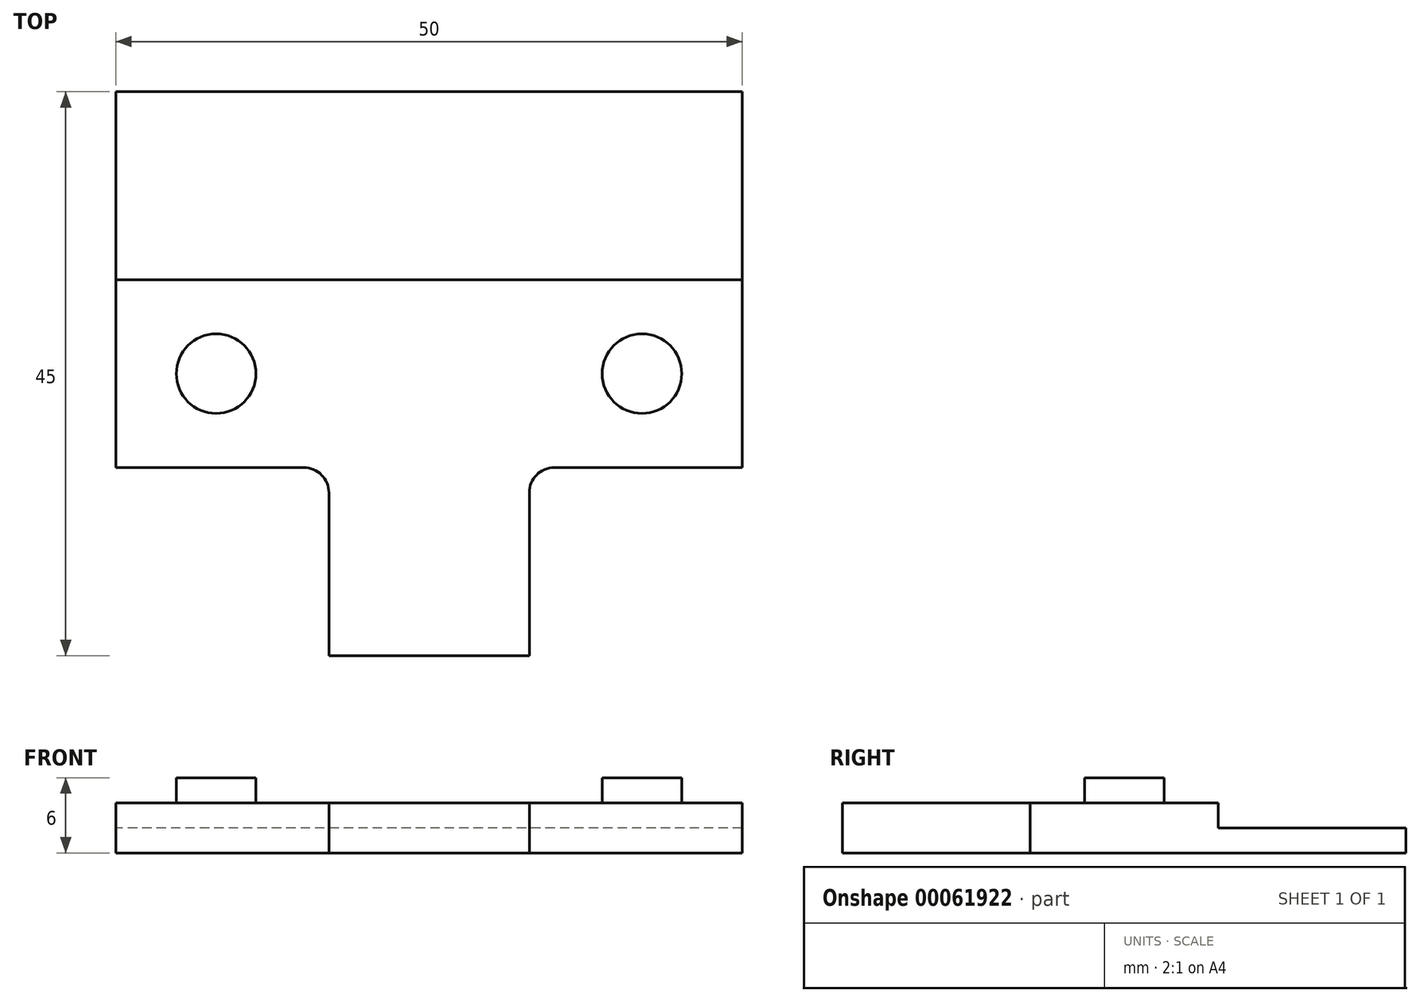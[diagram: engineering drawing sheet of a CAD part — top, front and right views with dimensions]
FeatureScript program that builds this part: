
annotation { "Feature Type Name" : "Feature", "Feature Type Description" : "" }
export const myFeature = defineFeature(function(context is Context, id is Id, definition is map)
    precondition{}
    {
        {
            var Q0;
            Q0=qCreatedBy(makeId("Top.planeOp"),FACE);
            var sketch = newSketch(context, id + "F0", { "sketchPlane" : qUnion([Q0])});
            skLineSegment(sketch, "E0.rect.bottom", {"start": v(8, -15) * mm, "end": v(-8, -15) * mm});
            skLineSegment(sketch, "E0.rect.top", {"start": v(25, 15) * mm, "end": v(-25, 15) * mm});
            skLineSegment(sketch, "E0.rect.left", {"start": v(25, 0) * mm, "end": v(25, 15) * mm});
            skLineSegment(sketch, "E0.rect.right", {"start": v(-25, 0) * mm, "end": v(-25, 15) * mm});
            skPoint(sketch, "E0.rect.middle", {"position": v(0, 0) * mm});
            skLineSegment(sketch, "E1", {"start": v(-25, 0) * mm, "end": v(-8, 0) * mm});
            skPoint(sketch, "E1.endSnap0", {"position": v(-25, 0) * mm});
            skLineSegment(sketch, "E2", {"start": v(-8, 0) * mm, "end": v(-8, -15) * mm});
            skLineSegment(sketch, "E3", {"start": v(25, 0) * mm, "end": v(8, 0) * mm});
            skPoint(sketch, "E3.endSnap0", {"position": v(25, 0) * mm});
            skLineSegment(sketch, "E4", {"start": v(8, 0) * mm, "end": v(8, -15) * mm});
            skPoint(sketch, "E5.orphan", {"position": v(-25, -15) * mm});
            skPoint(sketch, "E6.orphan", {"position": v(25, -15) * mm});
            skSolve(sketch);
        }
        {
            var Q0;
            Q0=makeQuery(id+"F0.imprint","IMPRINT",FACE,{"disambiguationData":[TD([[makeQuery(id+"F0.imprint","IMPRINT",EDGE,{"derivedFrom":sQuery(id+"F0.wireOp",EDGE,"E0.rect.bottom")}),-1.0]])]});
            extrude(context, id + "F1", {"entities" : qUnion([Q0]), "depth" : 2 * mm});
        }
        {
            var Q0;
            Q0=makeQuery(id+"F1.opExtrude","SWEPT_EDGE",EDGE,{"disambiguationData":[OSD([sQuery(id+"F0.wireOp",EDGE,"E1"),sQuery(id+"F0.wireOp",EDGE,"E2")])]});
            var Q1;
            Q1=makeQuery(id+"F1.opExtrude","SWEPT_EDGE",EDGE,{"disambiguationData":[OSD([sQuery(id+"F0.wireOp",EDGE,"E3"),sQuery(id+"F0.wireOp",EDGE,"E4")])]});
            fillet(context, id + "F2", {"entities" : qUnion([Q0, Q1]), "radius" : 2 * mm, "tangentPropagation" : true, "allowEdgeOverflow" : false});
        }
        {
            var Q0;
            Q0=makeQuery(id+"F1.opExtrude","CAP_FACE",FACE,{"disambiguationData":[OSD([sQuery(id+"F0.wireOp",EDGE,"E0.rect.bottom"),sQuery(id+"F0.wireOp",EDGE,"E0.rect.top"),sQuery(id+"F0.wireOp",EDGE,"E0.rect.left"),sQuery(id+"F0.wireOp",EDGE,"E0.rect.right"),sQuery(id+"F0.wireOp",EDGE,"E1"),sQuery(id+"F0.wireOp",EDGE,"E2"),sQuery(id+"F0.wireOp",EDGE,"E3"),sQuery(id+"F0.wireOp",EDGE,"E4")])],"isStart":false});
            var sketch = newSketch(context, id + "F3", { "sketchPlane" : qUnion([Q0])});
            skLineSegment(sketch, "E7", {"start": v(-25, 7.5) * mm, "end": v(-17, 7.5) * mm});
            skLineSegment(sketch, "E8", {"start": v(25, 7.5) * mm, "end": v(17, 7.5) * mm});
            skCircle(sketch, "E9", {"center": v(-17, 7.5) * mm, "radius": 3.17 * mm});
            skCircle(sketch, "E10", {"center": v(17, 7.5) * mm, "radius": 3.17 * mm});
            skSolve(sketch);
        }
        {
            var Q0;
            Q0=makeQuery(id+"F3.imprint","IMPRINT",FACE,{"disambiguationData":[TD([[makeQuery(id+"F3.imprint","IMPRINT",EDGE,{"derivedFrom":sQuery(id+"F3.wireOp",EDGE,"E9")}),1.0]])]});
            var Q1;
            Q1=makeQuery(id+"F3.imprint","IMPRINT",FACE,{"disambiguationData":[TD([[makeQuery(id+"F3.imprint","IMPRINT",EDGE,{"derivedFrom":sQuery(id+"F3.wireOp",EDGE,"E10")}),1.0]])]});
            extrude(context, id + "F4", {"entities" : qUnion([Q0, Q1]), "operationType" : NewBodyOperationType.ADD, "depth" : 2 * mm});
        }
        {
            var Q0;
            Q0=makeQuery(id+"F1.opExtrude","CAP_FACE",FACE,{"disambiguationData":[OSD([sQuery(id+"F0.wireOp",EDGE,"E0.rect.bottom"),sQuery(id+"F0.wireOp",EDGE,"E0.rect.top"),sQuery(id+"F0.wireOp",EDGE,"E0.rect.left"),sQuery(id+"F0.wireOp",EDGE,"E0.rect.right"),sQuery(id+"F0.wireOp",EDGE,"E1"),sQuery(id+"F0.wireOp",EDGE,"E2"),sQuery(id+"F0.wireOp",EDGE,"E3"),sQuery(id+"F0.wireOp",EDGE,"E4")])],"isStart":true});
            var sketch = newSketch(context, id + "F5", { "sketchPlane" : qUnion([Q0])});
            skLineSegment(sketch, "E11.0", {"start": v(8, 15) * mm, "end": v(-8, 15) * mm});
            skLineSegment(sketch, "E12.0", {"start": v(-8, 2) * mm, "end": v(-8, 15) * mm});
            skArc(sketch, "E13.0", {"start": v(-8, 2) * mm, "mid": v(-8.59, 0.59) * mm, "end": v(-10, 0) * mm});
            skLineSegment(sketch, "E14.0", {"start": v(-25, 0) * mm, "end": v(-10, 0) * mm});
            skLineSegment(sketch, "E15.0", {"start": v(8, 2) * mm, "end": v(8, 15) * mm});
            skArc(sketch, "E16.0", {"start": v(10, 0) * mm, "mid": v(8.59, 0.59) * mm, "end": v(8, 2) * mm});
            skLineSegment(sketch, "E17.0", {"start": v(25, 0) * mm, "end": v(10, 0) * mm});
            skLineSegment(sketch, "E18.0", {"start": v(25, 0) * mm, "end": v(25, -15) * mm});
            skLineSegment(sketch, "E19.0", {"start": v(-25, 0) * mm, "end": v(-25, -15) * mm});
            skLineSegment(sketch, "E20", {"start": v(-25, -15) * mm, "end": v(-25, -30) * mm});
            skLineSegment(sketch, "E21", {"start": v(-25, -30) * mm, "end": v(25, -30) * mm});
            skLineSegment(sketch, "E22", {"start": v(25, -30) * mm, "end": v(25, -15) * mm});
            skSolve(sketch);
        }
        {
            var Q0;
            Q0=makeQuery(id+"F5.imprint","IMPRINT",FACE,{"disambiguationData":[TD([[makeQuery(id+"F5.imprint","IMPRINT",EDGE,{"derivedFrom":sQuery(id+"F5.wireOp",EDGE,"E11.0")}),1.0]])]});
            var Q1;
            Q1=makeQuery(id+"F5.imprint","IMPRINT",FACE,{"disambiguationData":[TD([[makeQuery(id+"F5.imprint","IMPRINT",EDGE,{"derivedFrom":sQuery(id+"F5.wireOp",EDGE,"E20")}),1.0]])]});
            extrude(context, id + "F6", {"entities" : qUnion([Q0, Q1]), "operationType" : NewBodyOperationType.ADD, "depth" : 2 * mm});
        }
    });
